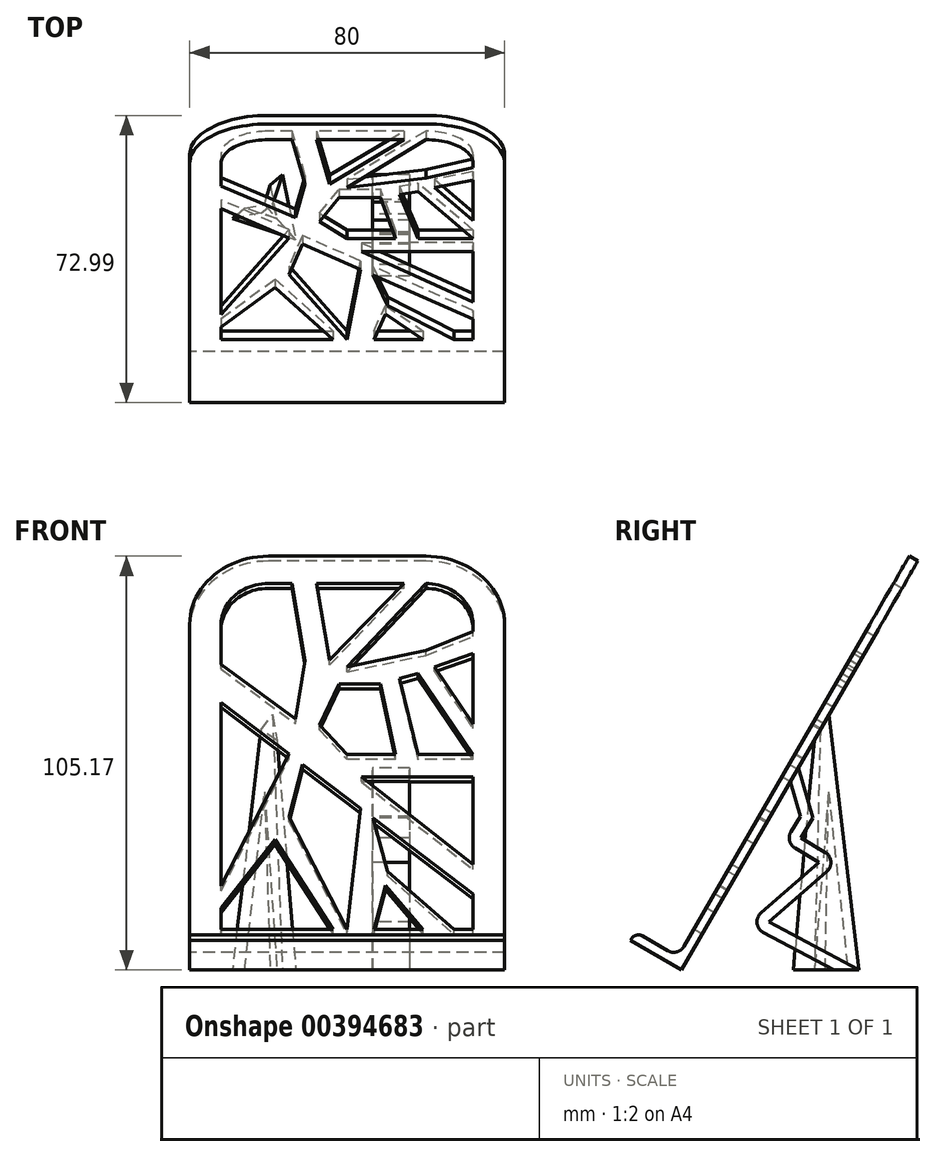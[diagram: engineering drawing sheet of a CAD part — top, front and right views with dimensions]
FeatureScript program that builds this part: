
annotation { "Feature Type Name" : "Feature", "Feature Type Description" : "" }
export const myFeature = defineFeature(function(context is Context, id is Id, definition is map)
    precondition{}
    {
        {
            var Q0;
            Q0=qCreatedBy(makeId("Right.planeOp"),FACE);
            var sketch = newSketch(context, id + "F0", { "sketchPlane" : qUnion([Q0])});
            skLineSegment(sketch, "E0", {"start": v(0, 0) * mm, "end": v(60, 103.92) * mm});
            skLineSegment(sketch, "E1", {"start": v(0, 0) * mm, "end": v(-13, 7.5) * mm});
            skLineSegment(sketch, "E2", {"start": v(0, 0) * mm, "end": v(58.09, 0) * mm, "construction": true});
            skLineSegment(sketch, "E3.0", {"start": v(-0.92, 3.42) * mm, "end": v(-11.74, 9.67) * mm});
            skLineSegment(sketch, "E3.1", {"start": v(-0.92, 3.42) * mm, "end": v(57.83, 105.17) * mm});
            skLineSegment(sketch, "E4", {"start": v(57.83, 105.17) * mm, "end": v(60, 103.92) * mm});
            skLineSegment(sketch, "E5", {"start": v(-11.74, 9.67) * mm, "end": v(-13, 7.5) * mm});
            skPoint(sketch, "E6.visualSharp", {"position": v(60, 103.92) * mm});
            skLineSegment(sketch, "E6.filletArc", {"start": v(60, 103.92) * mm, "end": v(60, 103.92) * mm});
            skPoint(sketch, "E7.visualSharp", {"position": v(57.83, 105.17) * mm});
            skLineSegment(sketch, "E7.filletArc", {"start": v(57.83, 105.17) * mm, "end": v(57.83, 105.17) * mm});
            skPoint(sketch, "E8.visualSharp", {"position": v(0, 0) * mm});
            skLineSegment(sketch, "E8.filletArc", {"start": v(0, 0) * mm, "end": v(0, 0) * mm});
            skPoint(sketch, "E9.visualSharp", {"position": v(-0.92, 3.42) * mm});
            skLineSegment(sketch, "E9.filletArc", {"start": v(-0.92, 3.42) * mm, "end": v(-0.92, 3.42) * mm});
            skPoint(sketch, "E10.visualSharp", {"position": v(-13, 7.5) * mm});
            skLineSegment(sketch, "E10.filletArc", {"start": v(-13, 7.5) * mm, "end": v(-13, 7.5) * mm});
            skPoint(sketch, "E11.visualSharp", {"position": v(-11.74, 9.67) * mm});
            skLineSegment(sketch, "E11.filletArc", {"start": v(-11.74, 9.67) * mm, "end": v(-11.74, 9.67) * mm});
            skSolve(sketch);
        }
        {
            var Q0;
            Q0 = qSketchRegion(id + "F0", true);
            extrude(context, id + "F1", {"entities" : qUnion([Q0]), "endBound" : BoundingType.SYMMETRIC, "depth" : 80 * mm});
        }
        {
            var Q0;
            Q0=makeQuery(id+"F1.opExtrude","CAP_EDGE",EDGE,{"disambiguationData":[OSD([sQuery(id+"F0.wireOp",EDGE,"E4")])],"isStart":false});
            fillet(context, id + "F2", {"entities" : qUnion([Q0]), "radius" : 20 * mm, "tangentPropagation" : true, "allowEdgeOverflow" : false});
        }
        {
            var Q0;
            Q0=makeQuery(id+"F1.opExtrude","CAP_EDGE",EDGE,{"disambiguationData":[OSD([sQuery(id+"F0.wireOp",EDGE,"E4")])],"isStart":true});
            fillet(context, id + "F3", {"entities" : qUnion([Q0]), "radius" : 20 * mm, "tangentPropagation" : true, "allowEdgeOverflow" : false});
        }
        {
            var Q0;
            Q0=makeQuery(id+"F1.opExtrude","SWEPT_FACE",FACE,{"disambiguationData":[OSD([sQuery(id+"F0.wireOp",EDGE,"E3.1")])]});
            var sketch = newSketch(context, id + "F4", { "sketchPlane" : qUnion([Q0])});
            skArc(sketch, "E12.0", {"start": v(32, 100) * mm, "mid": v(28.49, 108.49) * mm, "end": v(20, 112) * mm});
            skArc(sketch, "E12.1", {"start": v(-20, 112) * mm, "mid": v(-28.49, 108.49) * mm, "end": v(-32, 100) * mm});
            skLineSegment(sketch, "E12.2", {"start": v(-32, 100) * mm, "end": v(-32, 88.3) * mm});
            skLineSegment(sketch, "E12.3", {"start": v(14.44, 112) * mm, "end": v(-7.74, 112) * mm});
            skLineSegment(sketch, "E12.4", {"start": v(-32, 10.5) * mm, "end": v(-3.59, 10.5) * mm});
            skLineSegment(sketch, "E12.5", {"start": v(32, 10.5) * mm, "end": v(32, 20.92) * mm});
            skLineSegment(sketch, "E13", {"start": v(32, 20.92) * mm, "end": v(6.6, 43.2) * mm});
            skLineSegment(sketch, "E14", {"start": v(-32, 88.3) * mm, "end": v(-13.1, 72.29) * mm});
            skLineSegment(sketch, "E15", {"start": v(-13.1, 72.29) * mm, "end": v(-10.66, 89.48) * mm});
            skLineSegment(sketch, "E16", {"start": v(-10.66, 89.48) * mm, "end": v(-13.96, 112) * mm});
            skLineSegment(sketch, "E17", {"start": v(-7.74, 112) * mm, "end": v(-4.45, 89.55) * mm});
            skLineSegment(sketch, "E18", {"start": v(-4.45, 89.55) * mm, "end": v(14.44, 112) * mm});
            skLineSegment(sketch, "E19", {"start": v(32, 55.25) * mm, "end": v(3.62, 55.25) * mm});
            skPoint(sketch, "E19.endSnap0", {"position": v(32, 55.25) * mm});
            skLineSegment(sketch, "E20", {"start": v(3.62, 55.25) * mm, "end": v(32, 29.56) * mm});
            skLineSegment(sketch, "E21", {"start": v(20, 112) * mm, "end": v(0, 87.54) * mm});
            skLineSegment(sketch, "E22", {"start": v(0, 87.54) * mm, "end": v(20, 92.37) * mm});
            skLineSegment(sketch, "E23", {"start": v(20, 92.37) * mm, "end": v(32, 97.93) * mm});
            skLineSegment(sketch, "E24", {"start": v(32, 91.42) * mm, "end": v(22.15, 87.55) * mm});
            skLineSegment(sketch, "E25", {"start": v(22.15, 87.55) * mm, "end": v(32, 70.85) * mm});
            skLineSegment(sketch, "E26", {"start": v(32, 61.8) * mm, "end": v(17.99, 61.8) * mm});
            skLineSegment(sketch, "E27", {"start": v(-7.03, 70.42) * mm, "end": v(-2.02, 82.54) * mm});
            skLineSegment(sketch, "E28", {"start": v(-2.02, 82.54) * mm, "end": v(8.53, 82.54) * mm});
            skLineSegment(sketch, "E29.trimOffspring", {"start": v(-32, 77.06) * mm, "end": v(-32, 23.22) * mm});
            skLineSegment(sketch, "E30.trimOffspring", {"start": v(-13.96, 112) * mm, "end": v(-20, 112) * mm});
            skLineSegment(sketch, "E31.trimOffspring", {"start": v(32, 97.93) * mm, "end": v(32, 100) * mm});
            skLineSegment(sketch, "E32.trimOffspring", {"start": v(32, 70.85) * mm, "end": v(32, 91.42) * mm});
            skLineSegment(sketch, "E33.trimOffspring", {"start": v(32, 29.56) * mm, "end": v(32, 55.25) * mm});
            skLineSegment(sketch, "E34", {"start": v(-32, 23.22) * mm, "end": v(-14.8, 61.97) * mm});
            skLineSegment(sketch, "E35", {"start": v(-32, 16.74) * mm, "end": v(-18.32, 36.92) * mm});
            skLineSegment(sketch, "E36", {"start": v(-18.32, 36.92) * mm, "end": v(-3.59, 10.5) * mm});
            skLineSegment(sketch, "E37", {"start": v(-11.33, 58.93) * mm, "end": v(-14.75, 43.55) * mm});
            skLineSegment(sketch, "E38", {"start": v(-14.75, 43.55) * mm, "end": v(0, 10.5) * mm});
            skLineSegment(sketch, "E39", {"start": v(0, 10.5) * mm, "end": v(3.4, 46.01) * mm});
            skLineSegment(sketch, "E40.trimOffspring", {"start": v(-32, 16.74) * mm, "end": v(-32, 10.5) * mm});
            skLineSegment(sketch, "E41.trimOffspring", {"start": v(-14.8, 61.97) * mm, "end": v(-32, 77.06) * mm});
            skLineSegment(sketch, "E42.trimOffspring", {"start": v(6.8, 10.5) * mm, "end": v(19.34, 10.5) * mm});
            skLineSegment(sketch, "E43", {"start": v(6.6, 43.2) * mm, "end": v(10.32, 27.6) * mm});
            skLineSegment(sketch, "E44", {"start": v(10.32, 27.6) * mm, "end": v(27.15, 10.5) * mm});
            skLineSegment(sketch, "E45", {"start": v(6.8, 10.5) * mm, "end": v(9.75, 23.48) * mm});
            skLineSegment(sketch, "E46", {"start": v(9.75, 23.48) * mm, "end": v(19.34, 10.5) * mm});
            skLineSegment(sketch, "E47.trimOffspring", {"start": v(27.15, 10.5) * mm, "end": v(32, 10.5) * mm});
            skLineSegment(sketch, "E48.trimOffspring", {"start": v(3.4, 46.01) * mm, "end": v(-11.33, 58.93) * mm});
            skLineSegment(sketch, "E49", {"start": v(32, 61.8) * mm, "end": v(17.99, 85.57) * mm});
            skLineSegment(sketch, "E50", {"start": v(13.26, 84.05) * mm, "end": v(17.99, 85.57) * mm});
            skLineSegment(sketch, "E51", {"start": v(-7.03, 70.42) * mm, "end": v(0, 61.8) * mm});
            skLineSegment(sketch, "E52", {"start": v(12.3, 61.8) * mm, "end": v(8.53, 82.54) * mm});
            skLineSegment(sketch, "E53", {"start": v(13.26, 84.05) * mm, "end": v(17.99, 61.8) * mm});
            skLineSegment(sketch, "E54.trimOffspring", {"start": v(12.3, 61.8) * mm, "end": v(0, 61.8) * mm});
            skSolve(sketch);
        }
        {
            var Q0;
            Q0 = qSketchRegion(id + "F4", true);
            extrude(context, id + "F5", {"entities" : qUnion([Q0]), "operationType" : NewBodyOperationType.REMOVE, "oppositeDirection" : true, "depth" : 25 * mm});
        }
        {
            var Q0;
            Q0=makeQuery(id+"F1.opExtrude","SWEPT_EDGE",EDGE,{"disambiguationData":[OSD([sQuery(id+"F0.wireOp",EDGE,"E3.0"),sQuery(id+"F0.wireOp",EDGE,"E3.1")])]});
            fillet(context, id + "F6", {"entities" : qUnion([Q0]), "radius" : 3 * mm, "tangentPropagation" : true, "allowEdgeOverflow" : false});
        }
        {
            var Q0;
            Q0=makeQuery(id+"F1.opExtrude","SWEPT_EDGE",EDGE,{"disambiguationData":[OSD([sQuery(id+"F0.wireOp",EDGE,"E3.0"),sQuery(id+"F0.wireOp",EDGE,"E5")])]});
            fillet(context, id + "F7", {"entities" : qUnion([Q0]), "radius" : 2 * mm, "tangentPropagation" : true, "allowEdgeOverflow" : false});
        }
        {
            var Q0;
            Q0=qCreatedBy(makeId("Right.planeOp"),FACE);
            var sketch = newSketch(context, id + "F8", { "sketchPlane" : qUnion([Q0])});
            skLineSegment(sketch, "E55", {"start": v(29.38, 52.37) * mm, "end": v(33.4, 38.67) * mm});
            skLineSegment(sketch, "E56", {"start": v(33.4, 38.67) * mm, "end": v(30.34, 33.6) * mm});
            skLineSegment(sketch, "E57", {"start": v(30.34, 33.6) * mm, "end": v(36.46, 29.9) * mm});
            skLineSegment(sketch, "E58", {"start": v(36.88, 25.07) * mm, "end": v(22.14, 12.23) * mm});
            skLineSegment(sketch, "E59", {"start": v(22.14, 12.23) * mm, "end": v(45, 0) * mm});
            skLineSegment(sketch, "E60.0", {"start": v(20.72, 9.59) * mm, "end": v(38.64, 0) * mm});
            skLineSegment(sketch, "E60.1", {"start": v(27.44, 48.33) * mm, "end": v(30.15, 39.1) * mm});
            skLineSegment(sketch, "E60.2", {"start": v(30.15, 39.1) * mm, "end": v(27.77, 35.14) * mm});
            skLineSegment(sketch, "E60.3", {"start": v(28.8, 31.03) * mm, "end": v(34.91, 27.33) * mm});
            skLineSegment(sketch, "E60.4", {"start": v(34.91, 27.33) * mm, "end": v(20.17, 14.5) * mm});
            skLineSegment(sketch, "E61", {"start": v(45, 0) * mm, "end": v(38.64, 0) * mm});
            skLineSegment(sketch, "E62.0", {"start": v(0, 0) * mm, "end": v(50, 86.6) * mm});
            skLineSegment(sketch, "E63", {"start": v(29.38, 52.37) * mm, "end": v(27.44, 48.33) * mm});
            skPoint(sketch, "E64.visualSharp", {"position": v(16.9, 11.64) * mm});
            skArc(sketch, "E64.filletArc", {"start": v(20.17, 14.5) * mm, "mid": v(19.16, 11.9) * mm, "end": v(20.72, 9.59) * mm});
            skPoint(sketch, "E65.visualSharp", {"position": v(40, 27.78) * mm});
            skArc(sketch, "E65.filletArc", {"start": v(36.88, 25.07) * mm, "mid": v(37.9, 27.6) * mm, "end": v(36.46, 29.9) * mm});
            skPoint(sketch, "E66.visualSharp", {"position": v(26.22, 32.58) * mm});
            skArc(sketch, "E66.filletArc", {"start": v(27.77, 35.14) * mm, "mid": v(27.43, 32.87) * mm, "end": v(28.8, 31.03) * mm});
            skSolve(sketch);
        }
        {
            var Q0;
            Q0 = qSketchRegion(id + "F8", true);
            extrude(context, id + "F9", {"entities" : qUnion([Q0]), "operationType" : NewBodyOperationType.ADD, "depth" : 15.9 * mm});
        }
        {
            var Q0;
            Q0=qCreatedBy(makeId("Top.planeOp"),FACE);
            var sketch = newSketch(context, id + "F10", { "sketchPlane" : qUnion([Q0])});
            skCircle(sketch, "E67.cCircle", {"center": v(-19.54, 35.7) * mm, "radius": 4.9 * mm, "construction": true});
            skLineSegment(sketch, "E67.0", {"start": v(-29.16, 33.74) * mm, "end": v(-16.43, 45) * mm});
            skLineSegment(sketch, "E67.1", {"start": v(-16.43, 45) * mm, "end": v(-13.04, 28.36) * mm});
            skLineSegment(sketch, "E67.2", {"start": v(-13.04, 28.36) * mm, "end": v(-29.16, 33.74) * mm});
            skSolve(sketch);
        }
        {
            var Q0;
            Q0 = qSketchRegion(id + "F10", true);
            var Q1;
            Q1=makeQuery(id+"F1.opExtrude","SWEPT_FACE",FACE,{"disambiguationData":[OSD([sQuery(id+"F0.wireOp",EDGE,"E0")])]});
            extrude(context, id + "F11", {"entities" : qUnion([Q0]), "operationType" : NewBodyOperationType.ADD, "endBound" : BoundingType.UP_TO_SURFACE, "endBoundEntityFace" : qUnion([Q1]), "depth" : 25 * mm, "hasDraft" : true, "draftAngle" : 3.5 * degree, "draftPullDirection" : true});
        }
        {
            var Q0;
            Q0=makeQuery(id+"F11.opExtrude","CAP_FACE",FACE,{"disambiguationData":[OSD([sQuery(id+"F10.wireOp",EDGE,"E67.0"),sQuery(id+"F10.wireOp",EDGE,"E67.1"),sQuery(id+"F10.wireOp",EDGE,"E67.2")])],"isStart":true});
            var sketch = newSketch(context, id + "F12", { "sketchPlane" : qUnion([Q0])});
            skLineSegment(sketch, "E68.0", {"start": v(-17.81, -33.75) * mm, "end": v(-28.02, -37.16) * mm});
            skLineSegment(sketch, "E68.1", {"start": v(-19.96, -44.29) * mm, "end": v(-17.81, -33.75) * mm});
            skLineSegment(sketch, "E69", {"start": v(-19.96, -44.29) * mm, "end": v(-28.02, -37.16) * mm});
            skSolve(sketch);
        }
        {
            var Q0;
            Q0 = qSketchRegion(id + "F12", true);
            extrude(context, id + "F13", {"entities" : qUnion([Q0]), "operationType" : NewBodyOperationType.REMOVE, "oppositeDirection" : true, "depth" : 61.4 * mm, "hasDraft" : true, "draftAngle" : 3 * degree, "draftPullDirection" : true});
        }
        {
            var Q0;
            Q0=qCreatedBy(makeId("Right.planeOp"),FACE);
            var sketch = newSketch(context, id + "F14", { "sketchPlane" : qUnion([Q0])});
            skLineSegment(sketch, "E70.0.0", {"start": v(30.15, 39.1) * mm, "end": v(27.6, 47.8) * mm});
            skLineSegment(sketch, "E70.0.1", {"start": v(27.6, 47.8) * mm, "end": v(29.67, 51.39) * mm});
            skLineSegment(sketch, "E70.0.2", {"start": v(29.67, 51.39) * mm, "end": v(33.4, 38.67) * mm});
            skLineSegment(sketch, "E70.0.3", {"start": v(33.4, 38.67) * mm, "end": v(30.34, 33.6) * mm});
            skLineSegment(sketch, "E70.0.4", {"start": v(30.34, 33.6) * mm, "end": v(36.46, 29.9) * mm});
            skArc(sketch, "E70.0.5", {"start": v(36.46, 29.9) * mm, "mid": v(37.9, 27.6) * mm, "end": v(36.88, 25.07) * mm});
            skLineSegment(sketch, "E70.0.6", {"start": v(36.88, 25.07) * mm, "end": v(22.14, 12.23) * mm});
            skLineSegment(sketch, "E70.0.7", {"start": v(22.14, 12.23) * mm, "end": v(45, 0) * mm});
            skLineSegment(sketch, "E70.0.8", {"start": v(45, 0) * mm, "end": v(38.64, 0) * mm});
            skLineSegment(sketch, "E70.0.9", {"start": v(38.64, 0) * mm, "end": v(20.72, 9.59) * mm});
            skArc(sketch, "E70.0.10", {"start": v(20.72, 9.59) * mm, "mid": v(19.16, 11.9) * mm, "end": v(20.17, 14.5) * mm});
            skLineSegment(sketch, "E70.0.11", {"start": v(20.17, 14.5) * mm, "end": v(34.91, 27.33) * mm});
            skLineSegment(sketch, "E70.0.12", {"start": v(34.91, 27.33) * mm, "end": v(28.8, 31.03) * mm});
            skArc(sketch, "E70.0.13", {"start": v(28.8, 31.03) * mm, "mid": v(27.43, 32.87) * mm, "end": v(27.77, 35.14) * mm});
            skLineSegment(sketch, "E70.0.14", {"start": v(27.77, 35.14) * mm, "end": v(30.15, 39.1) * mm});
            skSolve(sketch);
        }
        {
            var Q0;
            Q0 = qSketchRegion(id + "F14", true);
            extrude(context, id + "F15", {"entities" : qUnion([Q0]), "operationType" : NewBodyOperationType.REMOVE, "depth" : 6.4 * mm});
        }
    });
